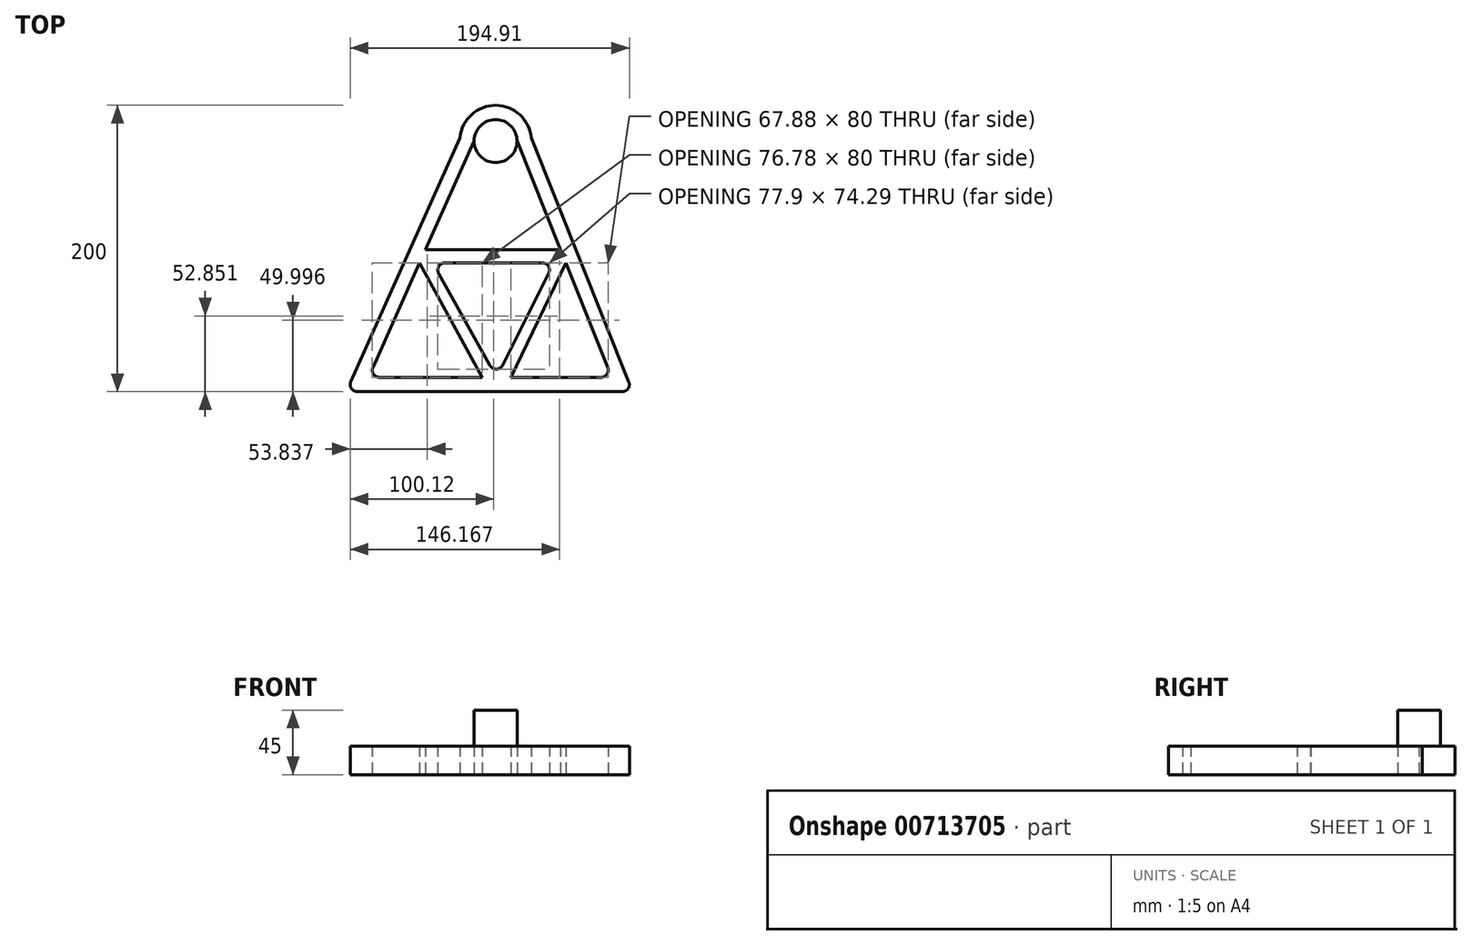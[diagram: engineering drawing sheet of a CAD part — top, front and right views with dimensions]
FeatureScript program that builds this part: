
annotation { "Feature Type Name" : "Feature", "Feature Type Description" : "" }
export const myFeature = defineFeature(function(context is Context, id is Id, definition is map)
    precondition{}
    {
        {
            var Q0;
            Q0=qCreatedBy(makeId("Top.planeOp"),FACE);
            var sketch = newSketch(context, id + "F0", { "sketchPlane" : qUnion([Q0])});
            skLineSegment(sketch, "E0.bottom", {"start": v(-27.2, 156.89) * mm, "end": v(-27, 156.89) * mm});
            skLineSegment(sketch, "E0.top", {"start": v(-108.07, -23.11) * mm, "end": v(46.63, -23.11) * mm});
            skPoint(sketch, "E1", {"position": v(-27.2, 156.89) * mm});
            skArc(sketch, "E2", {"start": v(-12, 141.89) * mm, "mid": v(-27, 156.89) * mm, "end": v(-42, 141.89) * mm});
            skPoint(sketch, "E3", {"position": v(-42, 141.89) * mm});
            skPoint(sketch, "E4", {"position": v(-12, 141.89) * mm});
            skLineSegment(sketch, "E5", {"start": v(-42, 141.89) * mm, "end": v(-112.63, -16.07) * mm});
            skLineSegment(sketch, "E6", {"start": v(-12, 141.89) * mm, "end": v(51.28, -16.26) * mm});
            skArc(sketch, "E7.0", {"start": v(-2.1, 144.05) * mm, "mid": v(-26.88, 166.89) * mm, "end": v(-51.89, 144.28) * mm});
            skLineSegment(sketch, "E7.1", {"start": v(-2.1, 144.05) * mm, "end": v(66.05, -26.26) * mm});
            skLineSegment(sketch, "E7.2", {"start": v(-123.5, -33.11) * mm, "end": v(61.4, -33.11) * mm});
            skLineSegment(sketch, "E7.3", {"start": v(-51.89, 144.28) * mm, "end": v(-128.06, -26.07) * mm});
            skPoint(sketch, "E8", {"position": v(-75.93, 66.01) * mm});
            skPoint(sketch, "E9", {"position": v(18.3, 66.17) * mm});
            skPoint(sketch, "E10", {"position": v(22, 56.89) * mm});
            skPoint(sketch, "E11", {"position": v(-80, 56.89) * mm});
            skLineSegment(sketch, "E12", {"start": v(-75.93, 66.01) * mm, "end": v(18.3, 66.17) * mm});
            skLineSegment(sketch, "E13", {"start": v(5.58, 56.89) * mm, "end": v(-62.33, 56.89) * mm});
            skPoint(sketch, "E14", {"position": v(-26.27, -23.11) * mm});
            skPoint(sketch, "E15", {"position": v(-36.27, -23.11) * mm});
            skPoint(sketch, "E16", {"position": v(-16.27, -23.11) * mm});
            skLineSegment(sketch, "E17", {"start": v(-66.7, 49.45) * mm, "end": v(-30.88, -14.84) * mm});
            skLineSegment(sketch, "E18", {"start": v(-80, 56.89) * mm, "end": v(-36.27, -23.11) * mm});
            skLineSegment(sketch, "E19", {"start": v(22, 56.89) * mm, "end": v(-16.27, -23.11) * mm});
            skLineSegment(sketch, "E20", {"start": v(10.05, 49.65) * mm, "end": v(-22.04, -14.64) * mm});
            skPoint(sketch, "E21.visualSharp", {"position": v(-131.2, -33.11) * mm});
            skArc(sketch, "E21.filletArc", {"start": v(-128.06, -26.07) * mm, "mid": v(-127.7, -30.83) * mm, "end": v(-123.5, -33.11) * mm});
            skPoint(sketch, "E22.visualSharp", {"position": v(68.8, -33.11) * mm});
            skArc(sketch, "E22.filletArc", {"start": v(61.4, -33.11) * mm, "mid": v(65.55, -30.92) * mm, "end": v(66.05, -26.26) * mm});
            skPoint(sketch, "E23.visualSharp", {"position": v(54.02, -23.11) * mm});
            skArc(sketch, "E23.filletArc", {"start": v(46.63, -23.11) * mm, "mid": v(50.77, -20.92) * mm, "end": v(51.28, -16.26) * mm});
            skPoint(sketch, "E24.visualSharp", {"position": v(-115.78, -23.11) * mm});
            skArc(sketch, "E24.filletArc", {"start": v(-112.63, -16.07) * mm, "mid": v(-112.27, -20.83) * mm, "end": v(-108.07, -23.11) * mm});
            skPoint(sketch, "E25", {"position": v(13.66, 56.89) * mm});
            skPoint(sketch, "E26", {"position": v(-70.84, 56.89) * mm});
            skArc(sketch, "E27.filletArc", {"start": v(-62.33, 56.89) * mm, "mid": v(-66.64, 54.42) * mm, "end": v(-66.7, 49.45) * mm});
            skArc(sketch, "E28.filletArc", {"start": v(10.05, 49.65) * mm, "mid": v(9.83, 54.52) * mm, "end": v(5.58, 56.89) * mm});
            skArc(sketch, "E29.filletArc", {"start": v(-30.88, -14.84) * mm, "mid": v(-26.4, -17.4) * mm, "end": v(-22.04, -14.64) * mm});
            skCircle(sketch, "E30", {"center": v(-27, 141.89) * mm, "radius": 15 * mm});
            skSolve(sketch);
        }
        {
            var Q0;
            Q0=makeQuery(id+"F0.imprint","IMPRINT",FACE,{"disambiguationData":[TD([[makeQuery(id+"F0.imprint","IMPRINT",EDGE,{"derivedFrom":sQuery(id+"F0.wireOp",EDGE,"E7.0")}),1.0]])]});
            var Q1;
            {var subQ3=sQuery(id+"F0.wireOp",EDGE,"E12");Q1=makeQuery(id+"F0.imprint","IMPRINT",FACE,{"disambiguationData":[TD([[makeQuery(id+"F0.imprint","IMPRINT",EDGE,{"derivedFrom":subQ3}),-1.0]])]});}
            var Q2;
            {var subQ0=sQuery(id+"F0.wireOp",EDGE,"E30");var subQ1=makeQuery(id+"F0.imprint","IMPRINT",VERTEX,{"derivedFrom":subQ0});Q2=makeQuery(id+"F0.imprint","IMPRINT",FACE,{"disambiguationData":[TD([[makeQuery(id+"F0.imprint","IMPRINT",EDGE,{"disambiguationData":[TD([[subQ1,1.0]])],"derivedFrom":subQ0}),1.0]])]});}
            extrude(context, id + "F1", {"entities" : qUnion([Q0, Q1, Q2]), "depth" : 20 * mm, "offsetDistance" : 25 * mm});
        }
        {
            var Q0;
            Q0=makeQuery(id+"F1.opExtrude","CAP_FACE",FACE,{"disambiguationData":[OSD([sQuery(id+"F0.wireOp",EDGE,"E0.top"),sQuery(id+"F0.wireOp",EDGE,"E5"),sQuery(id+"F0.wireOp",EDGE,"E6"),sQuery(id+"F0.wireOp",EDGE,"E7.0"),sQuery(id+"F0.wireOp",EDGE,"E7.1"),sQuery(id+"F0.wireOp",EDGE,"E7.2"),sQuery(id+"F0.wireOp",EDGE,"E7.3"),sQuery(id+"F0.wireOp",EDGE,"E12"),sQuery(id+"F0.wireOp",EDGE,"E13"),sQuery(id+"F0.wireOp",EDGE,"E17"),sQuery(id+"F0.wireOp",EDGE,"E18"),sQuery(id+"F0.wireOp",EDGE,"E19"),sQuery(id+"F0.wireOp",EDGE,"E20"),sQuery(id+"F0.wireOp",EDGE,"E21.filletArc"),sQuery(id+"F0.wireOp",EDGE,"E22.filletArc"),sQuery(id+"F0.wireOp",EDGE,"E23.filletArc"),sQuery(id+"F0.wireOp",EDGE,"E24.filletArc"),sQuery(id+"F0.wireOp",EDGE,"E27.filletArc"),sQuery(id+"F0.wireOp",EDGE,"E28.filletArc"),sQuery(id+"F0.wireOp",EDGE,"E29.filletArc"),sQuery(id+"F0.wireOp",EDGE,"E30")])],"isStart":false});
            var sketch = newSketch(context, id + "F2", { "sketchPlane" : qUnion([Q0])});
            skCircle(sketch, "E31", {"center": v(-27, 141.89) * mm, "radius": 15 * mm});
            skSolve(sketch);
        }
        {
            var Q0;
            Q0 = qSketchRegion(id + "F2", true);
            extrude(context, id + "F3", {"entities" : qUnion([Q0]), "operationType" : NewBodyOperationType.ADD, "depth" : 25 * mm, "offsetDistance" : 25 * mm});
        }
    });
